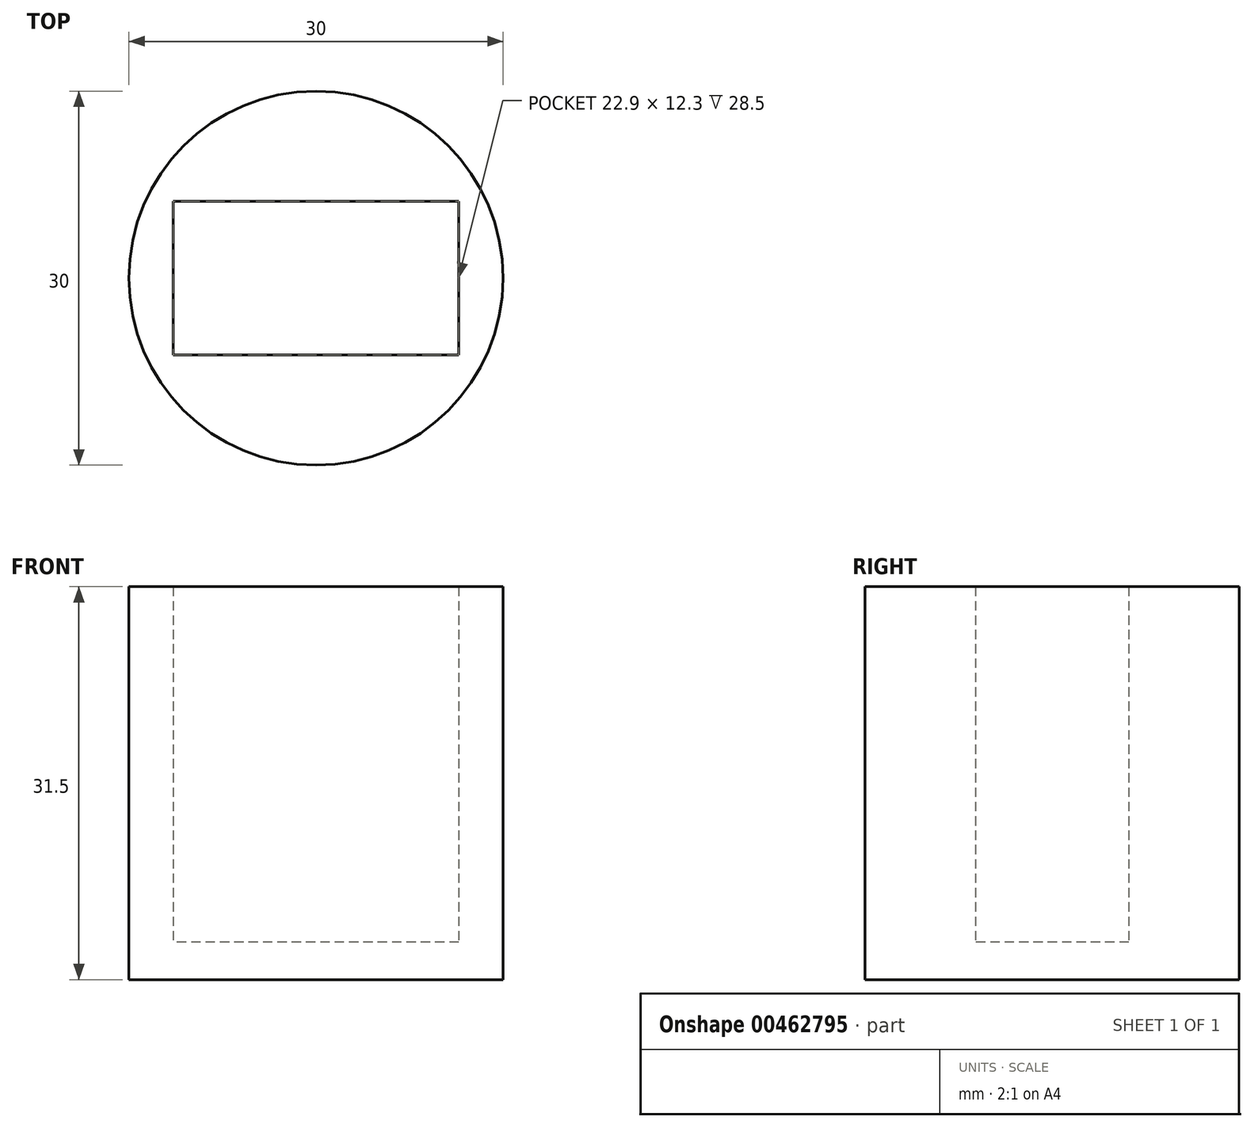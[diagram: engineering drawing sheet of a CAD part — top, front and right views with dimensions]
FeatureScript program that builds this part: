
annotation { "Feature Type Name" : "Feature", "Feature Type Description" : "" }
export const myFeature = defineFeature(function(context is Context, id is Id, definition is map)
    precondition{}
    {
        {
            var Q0;
            Q0=qCreatedBy(makeId("Top.planeOp"),FACE);
            var sketch = newSketch(context, id + "F0", { "sketchPlane" : qUnion([Q0])});
            skCircle(sketch, "E0", {"center": v(0, 0) * mm, "radius": 15 * mm});
            skLineSegment(sketch, "E1.bottom", {"start": v(11.45, 6.15) * mm, "end": v(-11.45, 6.15) * mm});
            skLineSegment(sketch, "E1.top", {"start": v(11.45, -6.15) * mm, "end": v(-11.45, -6.15) * mm});
            skLineSegment(sketch, "E1.left", {"start": v(11.45, 6.15) * mm, "end": v(11.45, -6.15) * mm});
            skLineSegment(sketch, "E1.right", {"start": v(-11.45, 6.15) * mm, "end": v(-11.45, -6.15) * mm});
            skSolve(sketch);
        }
        {
            var Q0;
            Q0=makeQuery(id+"F0.imprint","IMPRINT",FACE,{"disambiguationData":[TD([[makeQuery(id+"F0.imprint","IMPRINT",EDGE,{"derivedFrom":sQuery(id+"F0.wireOp",EDGE,"E0")}),1.0]])]});
            extrude(context, id + "F1", {"entities" : qUnion([Q0]), "depth" : 28.5 * mm});
        }
        {
            var Q0;
            Q0=makeQuery(id+"F1.opExtrude","CAP_FACE",FACE,{"disambiguationData":[OSD([sQuery(id+"F0.wireOp",EDGE,"E0"),sQuery(id+"F0.wireOp",EDGE,"E1.bottom"),sQuery(id+"F0.wireOp",EDGE,"E1.top"),sQuery(id+"F0.wireOp",EDGE,"E1.left"),sQuery(id+"F0.wireOp",EDGE,"E1.right")])],"isStart":true});
            var sketch = newSketch(context, id + "F2", { "sketchPlane" : qUnion([Q0])});
            skCircle(sketch, "E2", {"center": v(0, 0) * mm, "radius": 15 * mm});
            skSolve(sketch);
        }
        {
            var Q0;
            Q0 = qSketchRegion(id + "F2", true);
            extrude(context, id + "F3", {"entities" : qUnion([Q0]), "operationType" : NewBodyOperationType.ADD, "depth" : 3 * mm});
        }
    });
